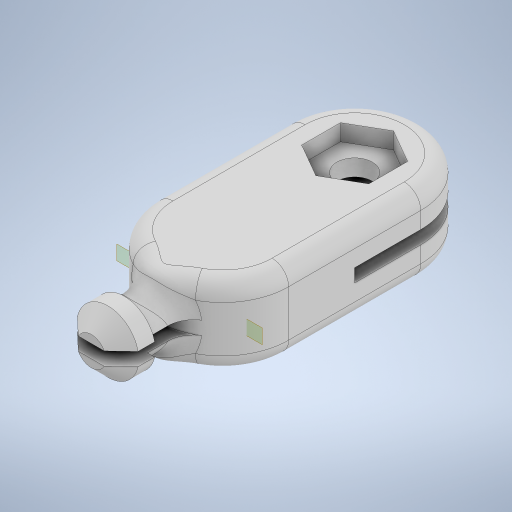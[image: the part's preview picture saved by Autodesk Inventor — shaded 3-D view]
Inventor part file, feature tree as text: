
AUTODESK INVENTOR PART (.ipt)
format: ipt  version: 2023.1 (Build 271208000, 208)  size: 428,032 bytes
history: native  units: mm
features: extrude x7, sketch x7, fillet x2, projected_geometry x2, plane x1, chamfer x1
ambient origin geometry x8: Origin, YZ Plane, XZ Plane, XY Plane, X Axis, Y Axis, Z Axis, Center Point
bodies: Solid1 (feature_tree)
feature tree (20):
  extrude  "Extrusion1"  Depth=8.0mm
  extrude  "Extrusion2"  Depth=2.0mm TaperAngle=0.0deg
  extrude  "Extrusion3"  Depth=4.0mm
  plane  "Work Plane1"
  extrude  "Extrusion4"  [1 undecoded]
  extrude  "Extrusion5"  Depth=5.95mm TaperAngle=0.0deg
  extrude  "Extrusion6"  Depth=3.75mm
  chamfer  "Chamfer1"  Distance=2.0mm
  fillet  "Fillet1"  Radius=2.0mm
  fillet  "Fillet2"  Radius=1.5mm
  extrude  "Extrusion7"  Depth=1.0mm
  sketch  "Sketch1"  dims[d0=4.0mm d1=8.0mm]
  sketch  "Sketch2"  dims[d2=2.15mm d3=2.0mm d4=0.0mm]
  sketch  "Sketch3"  dims[d5=0.8mm d6=0.0mm d7=4.0mm]
  sketch  "Sketch4"  dims[d8=2.0mm d9=0.0mm d10=-6.0mm]
  sketch  "Sketch6"  dims[d12=0.8mm d13=5.95mm d14=0.0mm]
  sketch  "Sketch7"  dims[d15=2.9mm d16=3.75mm d18=2.0mm d19=0.0mm d21=2.0mm d22=0.0mm]
  sketch  "Sketch8"  dims[d23=1.0mm d24=2.0mm d25=45.0deg d26=1.5mm d27=1.0mm d28=4.7mm d29=1.0mm d30=0.0mm d33=3.75mm d35=2.9mm]
  projected_geometry  "Projected Loop1"
  projected_geometry  "Projected Loop2"
note: 1 required parameter value undecoded (feature->parameter linkage not recoverable at this tier; creation-order binding heuristic only, values carry confidence <= 0.55)
